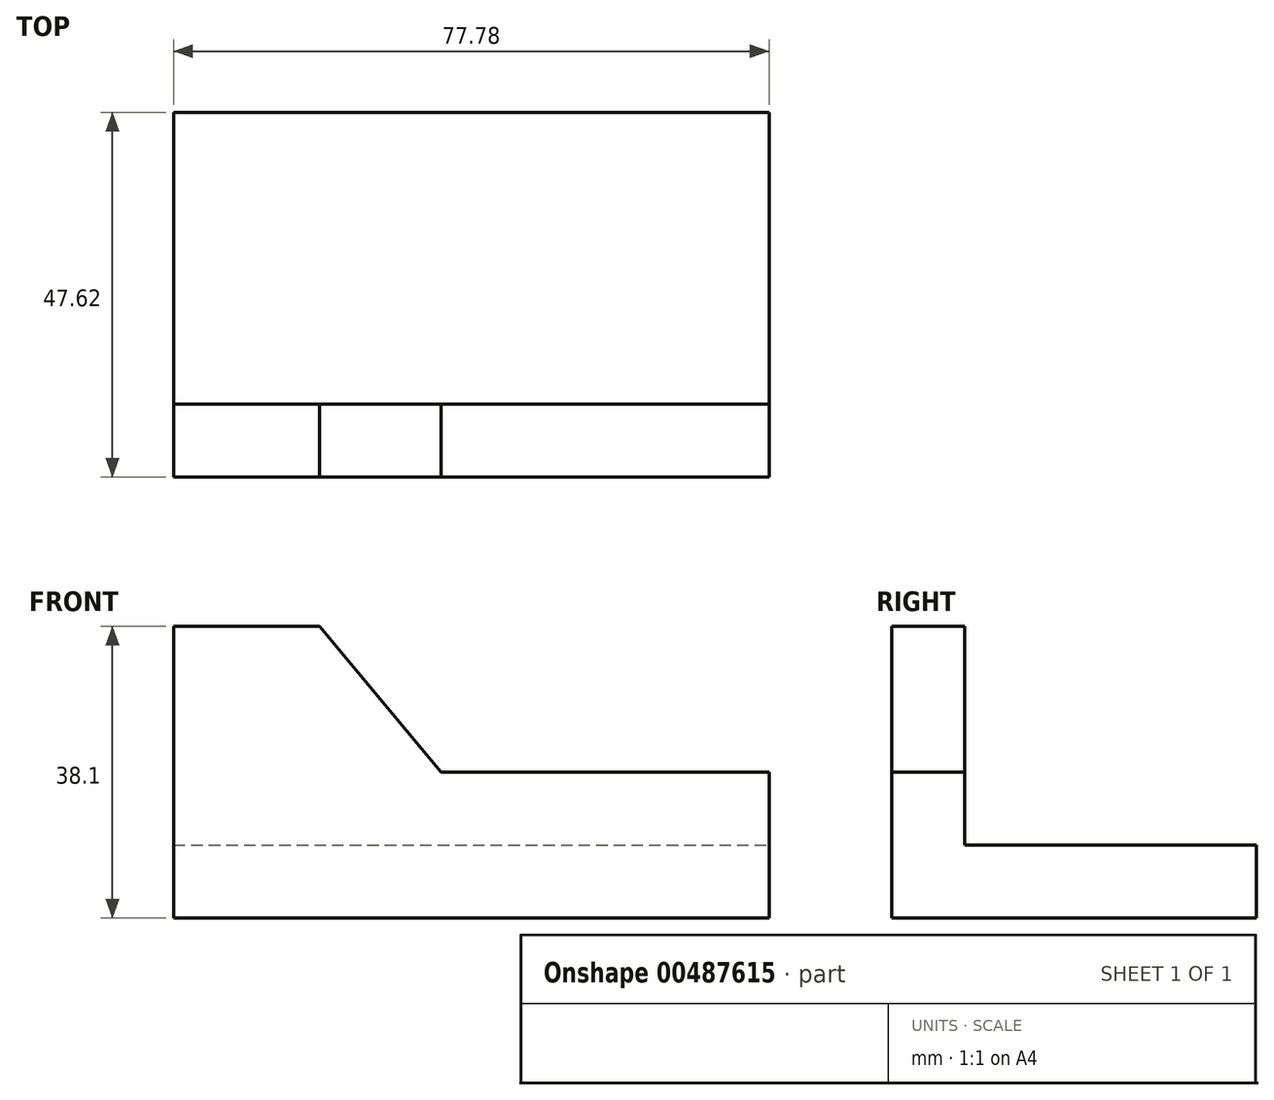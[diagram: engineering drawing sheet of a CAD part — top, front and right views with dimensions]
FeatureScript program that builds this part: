
annotation { "Feature Type Name" : "Feature", "Feature Type Description" : "" }
export const myFeature = defineFeature(function(context is Context, id is Id, definition is map)
    precondition{}
    {
        {
            var Q0;
            Q0=qCreatedBy(makeId("Top.planeOp"),FACE);
            var sketch = newSketch(context, id + "F0", { "sketchPlane" : qUnion([Q0])});
            skLineSegment(sketch, "E0.bottom", {"start": v(38.9, -23.81) * mm, "end": v(-38.9, -23.81) * mm});
            skLineSegment(sketch, "E0.top", {"start": v(38.9, 23.81) * mm, "end": v(-38.9, 23.81) * mm});
            skLineSegment(sketch, "E0.left", {"start": v(38.9, -23.81) * mm, "end": v(38.9, 23.81) * mm});
            skLineSegment(sketch, "E0.right", {"start": v(-38.9, -23.81) * mm, "end": v(-38.9, 23.81) * mm});
            skPoint(sketch, "E0.middle", {"position": v(0, 0) * mm});
            skSolve(sketch);
        }
        {
            var Q0;
            Q0 = qSketchRegion(id + "F0", true);
            extrude(context, id + "F1", {"entities" : qUnion([Q0]), "depth" : 9.52 * mm});
        }
        {
            var Q0;
            Q0=makeQuery(id+"F1.opExtrude","SWEPT_FACE",FACE,{"disambiguationData":[OSD([sQuery(id+"F0.wireOp",EDGE,"E0.bottom")])]});
            var sketch = newSketch(context, id + "F2", { "sketchPlane" : qUnion([Q0])});
            skLineSegment(sketch, "E1", {"start": v(-38.9, 0) * mm, "end": v(-38.9, 38.1) * mm});
            skLineSegment(sketch, "E2", {"start": v(-38.9, 38.1) * mm, "end": v(-19.84, 38.1) * mm});
            skLineSegment(sketch, "E3", {"start": v(-19.84, 38.1) * mm, "end": v(-3.97, 19.05) * mm});
            skLineSegment(sketch, "E4", {"start": v(-3.97, 19.05) * mm, "end": v(38.9, 19.05) * mm});
            skLineSegment(sketch, "E5", {"start": v(38.9, 19.05) * mm, "end": v(38.9, 9.53) * mm});
            skLineSegment(sketch, "E6", {"start": v(-38.9, 0) * mm, "end": v(38.9, 0) * mm});
            skLineSegment(sketch, "E7", {"start": v(38.9, 9.53) * mm, "end": v(38.9, 0) * mm});
            skSolve(sketch);
        }
        {
            var Q0;
            Q0 = qSketchRegion(id + "F2", true);
            extrude(context, id + "F3", {"entities" : qUnion([Q0]), "operationType" : NewBodyOperationType.ADD, "oppositeDirection" : true, "depth" : 9.52 * mm});
        }
    });
